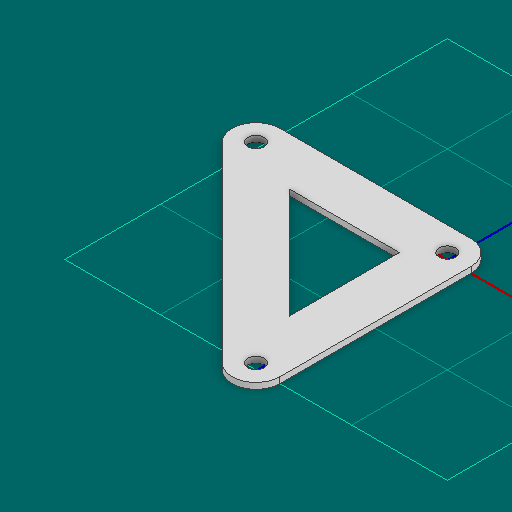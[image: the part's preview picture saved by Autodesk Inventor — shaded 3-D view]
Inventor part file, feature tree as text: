
AUTODESK INVENTOR PART (.ipt)
format: ipt  version: 2025 (Build 290162000, 162)  size: 110,080 bytes
history: native  units: in
note: dims shown in document units (in); Inventor stores cm internally (conversion verified against a paired STEP export)
features: other x3, extrude x1, sketch x1
ambient origin geometry x8: Origin, YZ Plane, XZ Plane, XY Plane, X Axis, Y Axis, Z Axis, Center Point
bodies: Solid1 (feature_tree)
feature tree (5):
  other  "Blocks"
  extrude  "Extrusion1"  Depth=0.0625in TaperAngle=0.0deg
  sketch  "Sketch1"  dims[d0=0.5in d1=0.5in d2=0.5in d3=0.0625in d4=0.0in d5=0.5in]
  other  "main"
  other  "main:1"
